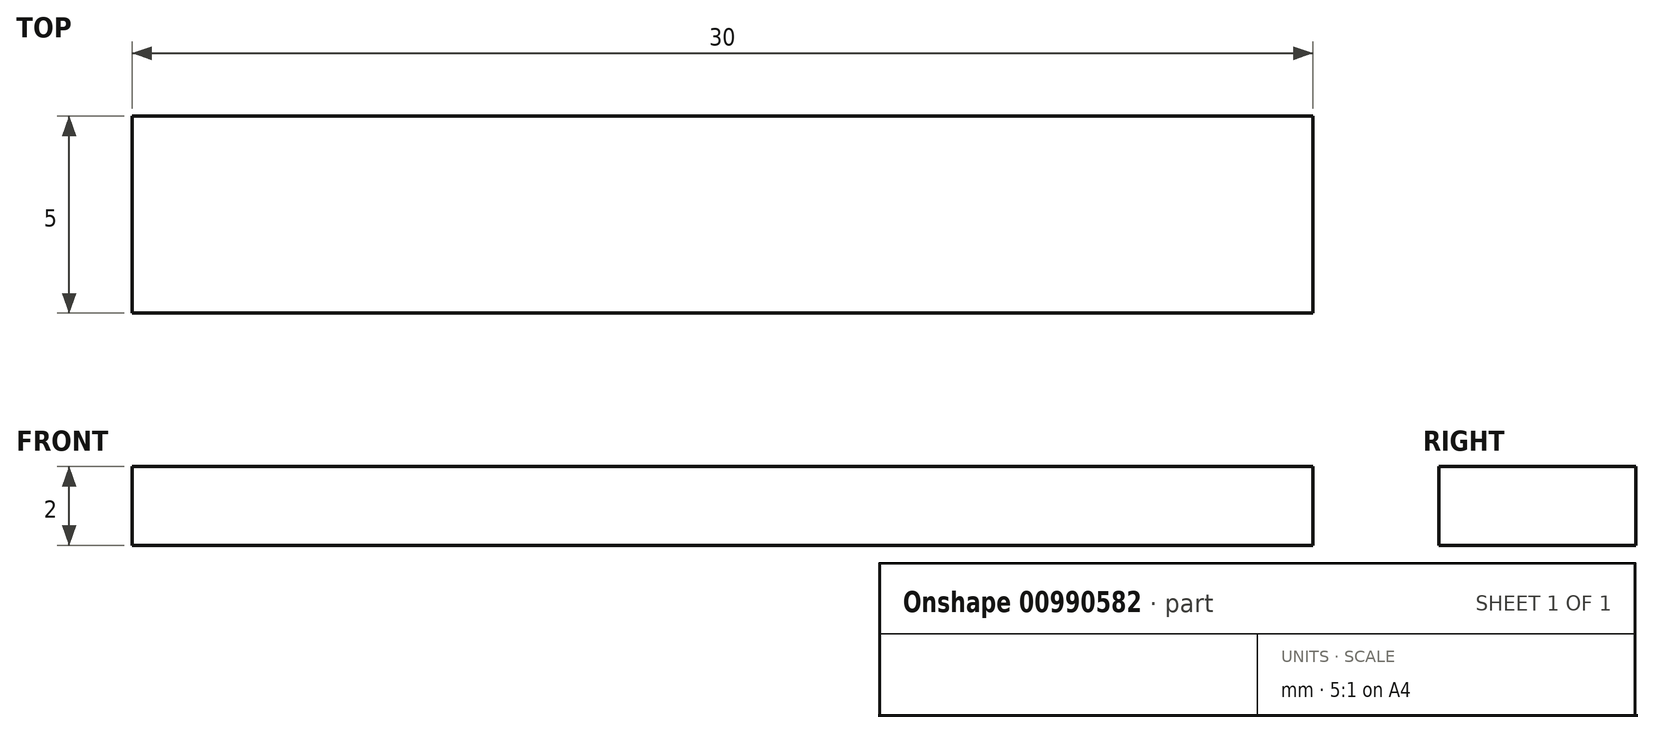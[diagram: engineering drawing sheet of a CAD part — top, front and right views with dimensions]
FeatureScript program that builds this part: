
annotation { "Feature Type Name" : "Feature", "Feature Type Description" : "" }
export const myFeature = defineFeature(function(context is Context, id is Id, definition is map)
    precondition{}
    {
        {
            var Q0;
            Q0=qCreatedBy(makeId("Top.planeOp"),FACE);
            var sketch = newSketch(context, id + "F0", { "sketchPlane" : qUnion([Q0])});
            skLineSegment(sketch, "E0.bottom", {"start": v(0, 0) * mm, "end": v(-30, 0) * mm});
            skLineSegment(sketch, "E0.top", {"start": v(0, 5) * mm, "end": v(-30, 5) * mm});
            skLineSegment(sketch, "E0.left", {"start": v(0, 0) * mm, "end": v(0, 5) * mm});
            skLineSegment(sketch, "E0.right", {"start": v(-30, 0) * mm, "end": v(-30, 5) * mm});
            skSolve(sketch);
        }
        {
            var Q0;
            Q0=makeQuery(id+"F0.imprint","IMPRINT",FACE,{"disambiguationData":[TD([[makeQuery(id+"F0.imprint","IMPRINT",EDGE,{"derivedFrom":sQuery(id+"F0.wireOp",EDGE,"E0.bottom")}),-1.0]])]});
            extrude(context, id + "F1", {"entities" : qUnion([Q0]), "depth" : 2 * mm, "offsetDistance" : 25 * mm});
        }
    });
